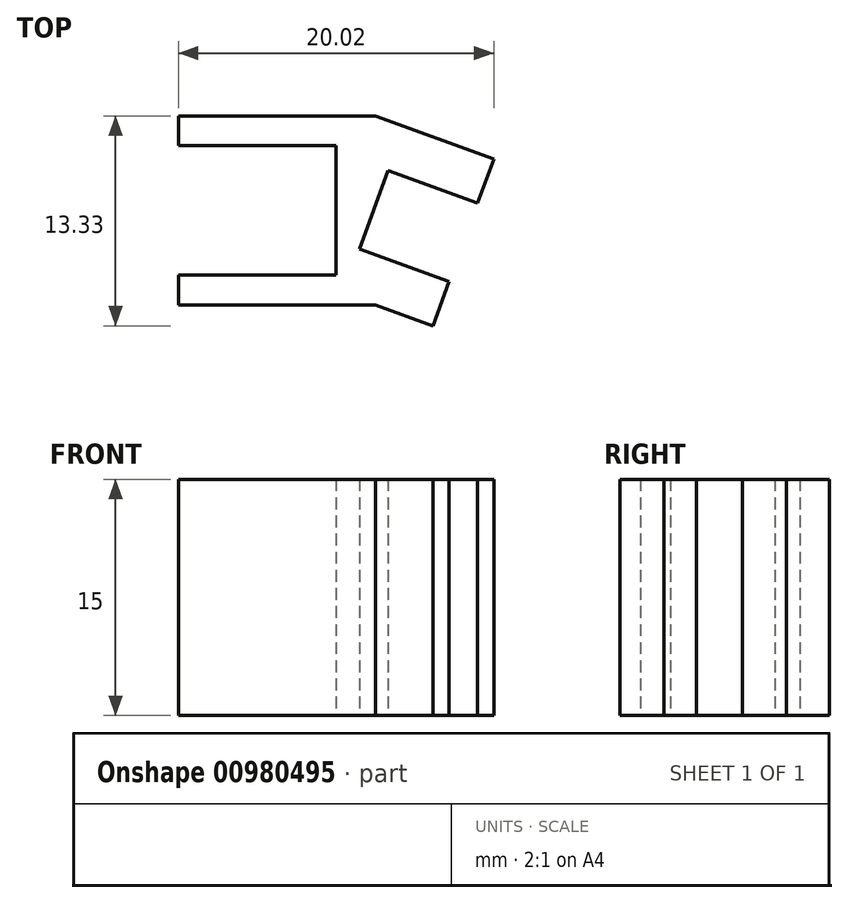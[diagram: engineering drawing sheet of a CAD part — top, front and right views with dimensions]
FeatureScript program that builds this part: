
annotation { "Feature Type Name" : "Feature", "Feature Type Description" : "" }
export const myFeature = defineFeature(function(context is Context, id is Id, definition is map)
    precondition{}
    {
        {
            var Q0;
            Q0=qCreatedBy(makeId("Top.planeOp"),FACE);
            var sketch = newSketch(context, id + "F0", { "sketchPlane" : qUnion([Q0])});
            skLineSegment(sketch, "E0.bottom", {"start": v(0, 0) * mm, "end": v(-12.5, 0) * mm});
            skLineSegment(sketch, "E0.top", {"start": v(0, 12) * mm, "end": v(-12.5, 12) * mm});
            skLineSegment(sketch, "E0.left", {"start": v(0, 0) * mm, "end": v(0, 12) * mm});
            skLineSegment(sketch, "E0.right", {"start": v(-12.5, 0) * mm, "end": v(-12.5, 12) * mm});
            skLineSegment(sketch, "E1", {"start": v(0, 12) * mm, "end": v(7.52, 9.26) * mm});
            skLineSegment(sketch, "E2", {"start": v(7.52, 9.26) * mm, "end": v(3.66, -1.33) * mm});
            skLineSegment(sketch, "E3", {"start": v(3.66, -1.33) * mm, "end": v(0, 0) * mm});
            skSolve(sketch);
        }
        {
            var Q0;
            Q0=makeQuery(id+"F0.imprint","IMPRINT",FACE,{"disambiguationData":[TD([[makeQuery(id+"F0.imprint","IMPRINT",EDGE,{"derivedFrom":sQuery(id+"F0.wireOp",EDGE,"E0.bottom")}),-1.0]])]});
            var Q1;
            Q1=makeQuery(id+"F0.imprint","IMPRINT",FACE,{"disambiguationData":[TD([[makeQuery(id+"F0.imprint","IMPRINT",EDGE,{"derivedFrom":sQuery(id+"F0.wireOp",EDGE,"E0.left")}),-1.0]])]});
            extrude(context, id + "F1", {"entities" : qUnion([Q0, Q1]), "depth" : 15 * mm, "offsetDistance" : 25 * mm});
        }
        {
            var Q0;
            Q0=makeQuery(id+"F1.opExtrude","SWEPT_FACE",FACE,{"disambiguationData":[OSD([sQuery(id+"F0.wireOp",EDGE,"E0.right")])]});
            var sketch = newSketch(context, id + "F2", { "sketchPlane" : qUnion([Q0])});
            skLineSegment(sketch, "E4", {"start": v(-10.1, 15) * mm, "end": v(-10.1, 0) * mm});
            skLineSegment(sketch, "E5", {"start": v(-1.9, 15) * mm, "end": v(-1.9, 0) * mm});
            skLineSegment(sketch, "E6", {"start": v(-12, 11.45) * mm, "end": v(-10.1, 11.45) * mm, "construction": true});
            skLineSegment(sketch, "E7", {"start": v(-1.9, 3.32) * mm, "end": v(0, 3.32) * mm, "construction": true});
            skSolve(sketch);
        }
        {
            var Q0;
            {var subQ0=sQuery(id+"F2.wireOp",EDGE,"E4");Q0=makeQuery(id+"F2.imprint","IMPRINT",FACE,{"disambiguationData":[TD([[makeQuery(id+"F2.imprint","IMPRINT",EDGE,{"derivedFrom":subQ0}),1.0]])]});}
            extrude(context, id + "F3", {"entities" : qUnion([Q0]), "operationType" : NewBodyOperationType.REMOVE, "oppositeDirection" : true, "depth" : 10 * mm, "offsetDistance" : 25 * mm});
        }
        {
            var Q0;
            Q0=makeQuery(id+"F1.opExtrude","SWEPT_FACE",FACE,{"disambiguationData":[OSD([sQuery(id+"F0.wireOp",EDGE,"E2")])]});
            var sketch = newSketch(context, id + "F4", { "sketchPlane" : qUnion([Q0])});
            skLineSegment(sketch, "E8", {"start": v(2.99, 15) * mm, "end": v(2.99, 0) * mm});
            skLineSegment(sketch, "E9", {"start": v(8.29, 15) * mm, "end": v(8.29, 0) * mm});
            skLineSegment(sketch, "E10", {"start": v(0, 12.89) * mm, "end": v(2.99, 12.89) * mm, "construction": true});
            skLineSegment(sketch, "E11", {"start": v(8.29, 2.9) * mm, "end": v(11.28, 2.9) * mm, "construction": true});
            skSolve(sketch);
        }
        {
            var Q0;
            {var subQ0=sQuery(id+"F4.wireOp",EDGE,"E8");Q0=makeQuery(id+"F4.imprint","IMPRINT",FACE,{"disambiguationData":[TD([[makeQuery(id+"F4.imprint","IMPRINT",EDGE,{"derivedFrom":subQ0}),1.0]])]});}
            extrude(context, id + "F5", {"entities" : qUnion([Q0]), "operationType" : NewBodyOperationType.REMOVE, "oppositeDirection" : true, "depth" : 6.05 * mm, "offsetDistance" : 25 * mm});
        }
    });
